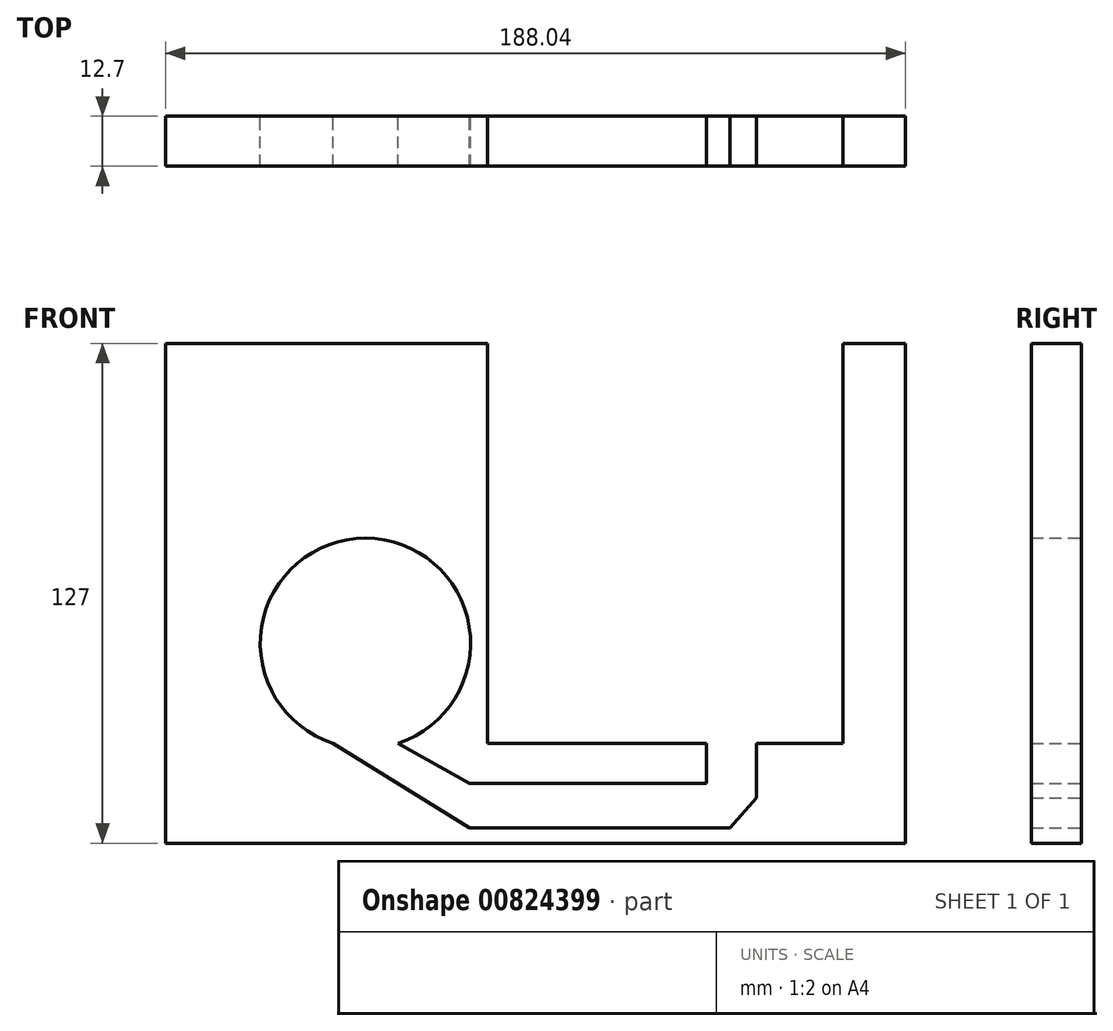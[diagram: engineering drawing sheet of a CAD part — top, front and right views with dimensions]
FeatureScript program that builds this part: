
annotation { "Feature Type Name" : "Feature", "Feature Type Description" : "" }
export const myFeature = defineFeature(function(context is Context, id is Id, definition is map)
    precondition{}
    {
        {
            var Q0;
            Q0=qCreatedBy(makeId("Front.planeOp"),FACE);
            var sketch = newSketch(context, id + "F0", { "sketchPlane" : qUnion([Q0])});
            skLineSegment(sketch, "E0", {"start": v(-90.94, 101.6) * mm, "end": v(-90.94, -25.4) * mm});
            skLineSegment(sketch, "E1", {"start": v(-90.94, -25.4) * mm, "end": v(97.1, -25.4) * mm});
            skLineSegment(sketch, "E2", {"start": v(97.1, -25.4) * mm, "end": v(97.1, 101.6) * mm});
            skLineSegment(sketch, "E3", {"start": v(97.1, 101.6) * mm, "end": v(81.23, 101.6) * mm});
            skLineSegment(sketch, "E4", {"start": v(81.23, 101.6) * mm, "end": v(81.23, 0) * mm});
            skLineSegment(sketch, "E5", {"start": v(81.23, 0) * mm, "end": v(59.26, 0) * mm});
            skLineSegment(sketch, "E6", {"start": v(59.26, 0) * mm, "end": v(59.26, -13.88) * mm});
            skLineSegment(sketch, "E7", {"start": v(59.26, -13.88) * mm, "end": v(52.47, -21.48) * mm});
            skLineSegment(sketch, "E8", {"start": v(-90.94, 101.6) * mm, "end": v(-9.13, 101.6) * mm});
            skLineSegment(sketch, "E9", {"start": v(-9.13, 101.6) * mm, "end": v(-9.13, 0) * mm});
            skLineSegment(sketch, "E10", {"start": v(-9.13, 0) * mm, "end": v(46.56, 0) * mm});
            skLineSegment(sketch, "E11", {"start": v(46.56, 0) * mm, "end": v(46.56, -10.2) * mm});
            skLineSegment(sketch, "E12", {"start": v(46.56, -10.2) * mm, "end": v(-13.74, -10.2) * mm});
            skLineSegment(sketch, "E13", {"start": v(-13.74, -10.2) * mm, "end": v(-31.87, 0) * mm});
            skLineSegment(sketch, "E14", {"start": v(52.47, -21.48) * mm, "end": v(-13.74, -21.48) * mm});
            skLineSegment(sketch, "E15", {"start": v(-13.74, -21.48) * mm, "end": v(-48.4, 0) * mm});
            skArc(sketch, "E16", {"start": v(-31.87, 0) * mm, "mid": v(-40.14, 52.11) * mm, "end": v(-48.4, 0) * mm});
            skSolve(sketch);
        }
        {
            var Q0;
            Q0 = qSketchRegion(id + "F0", true);
            extrude(context, id + "F1", {"entities" : qUnion([Q0]), "depth" : 12.7 * mm, "offsetDistance" : 25.4 * mm});
        }
    });
